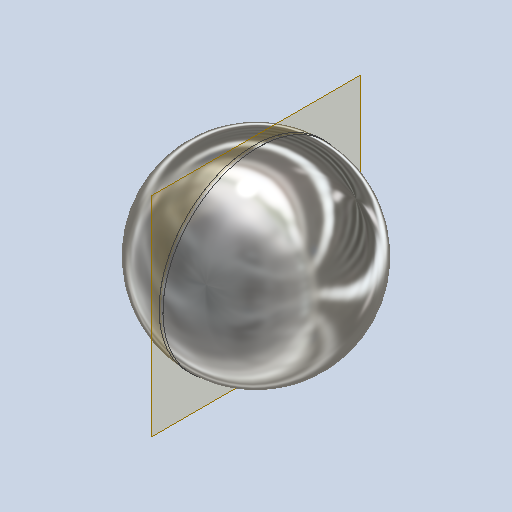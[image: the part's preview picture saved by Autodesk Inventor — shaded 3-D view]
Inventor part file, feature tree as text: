
AUTODESK INVENTOR PART (.ipt)
format: ipt  version: 2023 (Build 270158000, 158)  size: 217,088 bytes
history: native  units: mm
features: sketch x2, revolve x1, plane x1, extrude x1, other x1
ambient origin geometry x8: Origin, YZ Plane, XZ Plane, XY Plane, X Axis, Y Axis, Z Axis, Center Point
bodies: Volumenkörper1 (feature_tree)
feature tree (6):
  revolve  "Umdrehung1"
  plane  "Work Plane1"
  extrude  "Extrusion1"  TaperAngle=90.0deg  [1 undecoded]
  sketch  "Skizze1"  dims[d0=5.0mm d1=90.0deg]
  other  "Work Point1"
  sketch  "Sketch2"  dims[d8=0.1mm d9=0.0mm]
note: 1 required parameter value undecoded (feature->parameter linkage not recoverable at this tier; creation-order binding heuristic only, values carry confidence <= 0.55)
